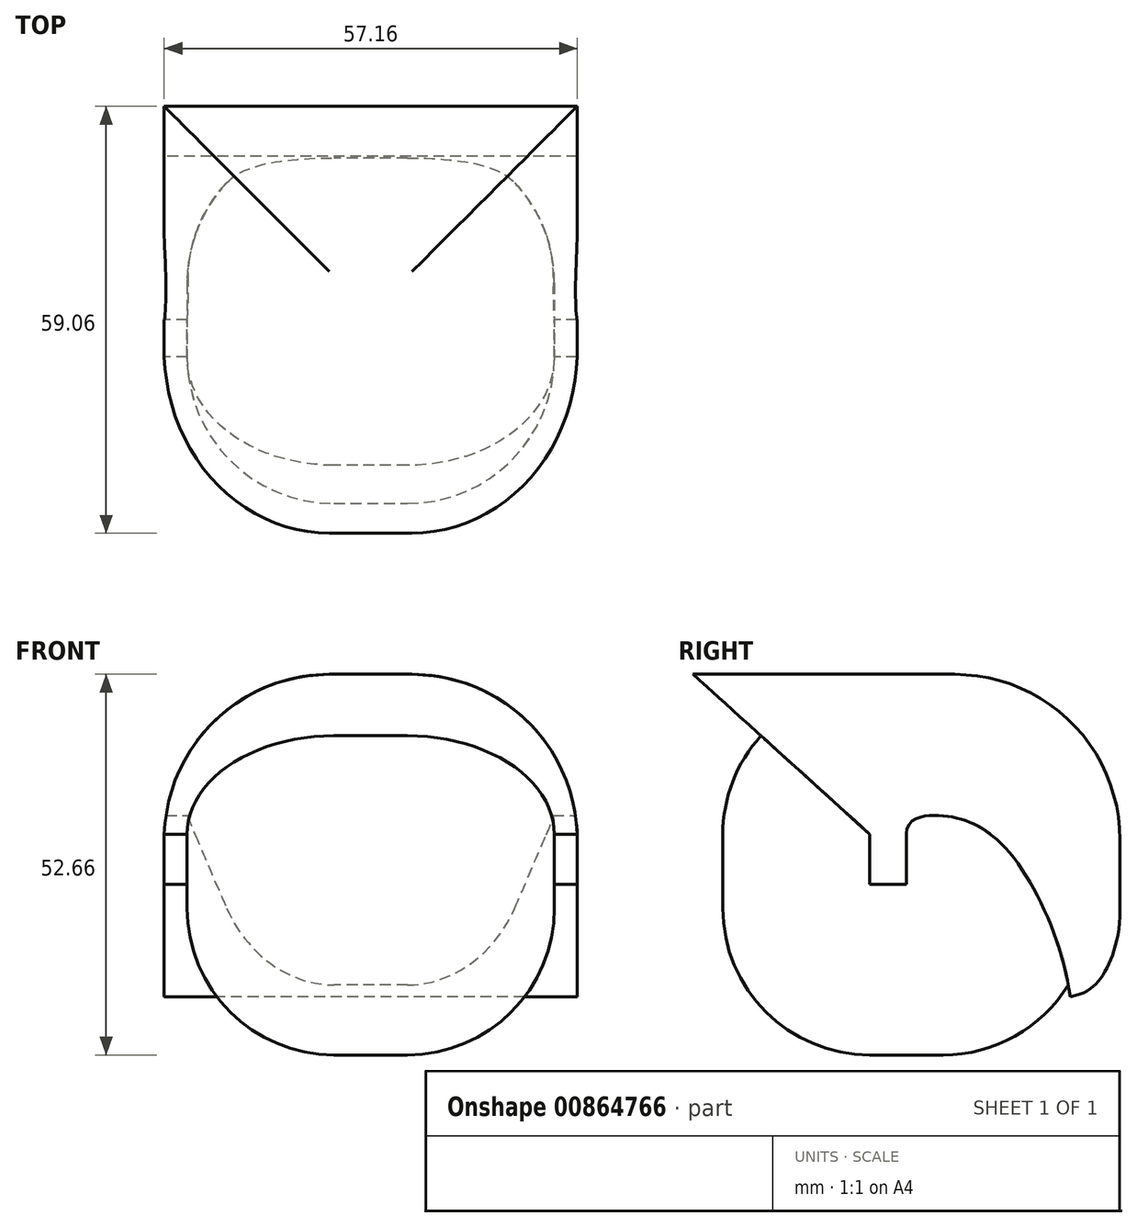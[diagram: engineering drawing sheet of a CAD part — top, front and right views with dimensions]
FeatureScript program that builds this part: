
annotation { "Feature Type Name" : "Feature", "Feature Type Description" : "" }
export const myFeature = defineFeature(function(context is Context, id is Id, definition is map)
    precondition{}
    {
        {
            var Q0;
            Q0=qCreatedBy(makeId("Top.planeOp"),FACE);
            var sketch = newSketch(context, id + "F0", { "sketchPlane" : qUnion([Q0])});
            skLineSegment(sketch, "E0.bottom", {"start": v(-25.4, 25.4) * mm, "end": v(25.4, 25.4) * mm});
            skLineSegment(sketch, "E0.top", {"start": v(-25.4, -25.4) * mm, "end": v(25.4, -25.4) * mm});
            skLineSegment(sketch, "E0.left", {"start": v(-25.4, 25.4) * mm, "end": v(-25.4, -25.4) * mm});
            skLineSegment(sketch, "E0.right", {"start": v(25.4, 25.4) * mm, "end": v(25.4, -25.4) * mm});
            skPoint(sketch, "E0.middle", {"position": v(0, 0) * mm});
            skSolve(sketch);
        }
        {
            var Q0;
            Q0 = qSketchRegion(id + "F0", true);
            extrude(context, id + "F1", {"entities" : qUnion([Q0]), "depth" : 50.8 * mm, "offsetDistance" : 25.4 * mm});
        }
        {
            var Q0;
            Q0=makeQuery(id+"F1.opExtrude","CAP_FACE",FACE,{"disambiguationData":[OSD([sQuery(id+"F0.wireOp",EDGE,"E0.bottom"),sQuery(id+"F0.wireOp",EDGE,"E0.top"),sQuery(id+"F0.wireOp",EDGE,"E0.left"),sQuery(id+"F0.wireOp",EDGE,"E0.right")])],"isStart":false});
            var Q1;
            Q1=makeQuery(id+"F1.opExtrude","SWEPT_FACE",FACE,{"disambiguationData":[OSD([sQuery(id+"F0.wireOp",EDGE,"E0.left")])]});
            var Q2;
            Q2=makeQuery(id+"F1.opExtrude","SWEPT_FACE",FACE,{"disambiguationData":[OSD([sQuery(id+"F0.wireOp",EDGE,"E0.top")])]});
            var Q3;
            Q3=makeQuery(id+"F1.opExtrude","SWEPT_FACE",FACE,{"disambiguationData":[OSD([sQuery(id+"F0.wireOp",EDGE,"E0.right")])]});
            var Q4;
            Q4=makeQuery(id+"F1.opExtrude","CAP_FACE",FACE,{"disambiguationData":[OSD([sQuery(id+"F0.wireOp",EDGE,"E0.bottom"),sQuery(id+"F0.wireOp",EDGE,"E0.top"),sQuery(id+"F0.wireOp",EDGE,"E0.left"),sQuery(id+"F0.wireOp",EDGE,"E0.right")])],"isStart":true});
            var Q5;
            Q5=makeQuery(id+"F1.opExtrude","SWEPT_FACE",FACE,{"disambiguationData":[OSD([sQuery(id+"F0.wireOp",EDGE,"E0.bottom")])]});
            fillet(context, id + "F2", {"entities" : qUnion([Q0, Q1, Q2, Q3, Q4, Q5]), "radius" : 20.32 * mm, "tangentPropagation" : true, "allowEdgeOverflow" : false});
        }
        {
            var Q0;
            Q0=qCreatedBy(makeId("Right.planeOp"),FACE);
            var sketch = newSketch(context, id + "F3", { "sketchPlane" : qUnion([Q0])});
            skLineSegment(sketch, "E1", {"start": v(0, 30.65) * mm, "end": v(0, 23.59) * mm});
            skLineSegment(sketch, "E2", {"start": v(0, 23.59) * mm, "end": v(-5.1, 23.59) * mm});
            skLineSegment(sketch, "E3", {"start": v(-5.1, 23.59) * mm, "end": v(-5.1, 30.55) * mm});
            skFitSpline(sketch, "E4", {"points": [v(0, 30.65) * mm, v(5.8, 33) * mm, v(14.64, 27.5) * mm, v(22.66, 8.04) * mm], "startDerivative": vector(0, 30.14) * mm, "endDerivative": vector(6.46, -47.47) * mm});
            skFitSpline(sketch, "E5", {"points": [v(22.66, 8.04) * mm, v(27.11, 11) * mm, v(29.54, 20.04) * mm], "startDerivative": vector(17.15, 3.72) * mm, "endDerivative": vector(0.03, 21.31) * mm});
            skLineSegment(sketch, "E6", {"start": v(29.54, 20.04) * mm, "end": v(29.54, 52.66) * mm});
            skLineSegment(sketch, "E7", {"start": v(29.54, 52.66) * mm, "end": v(-29.52, 52.66) * mm});
            skLineSegment(sketch, "E8", {"start": v(-5.1, 30.55) * mm, "end": v(-29.52, 52.66) * mm});
            skSolve(sketch);
        }
        {
            var Q0;
            Q0 = qSketchRegion(id + "F3", true);
            extrude(context, id + "F4", {"entities" : qUnion([Q0]), "operationType" : NewBodyOperationType.ADD, "depth" : 28.57 * mm, "offsetDistance" : 25.4 * mm, "hasSecondDirection" : true, "secondDirectionOppositeDirection" : true, "secondDirectionDepth" : 28.57 * mm});
        }
        {
            var Q0;
            Q0=makeQuery(id+"F4.opExtrude","SWEPT_EDGE",EDGE,{"disambiguationData":[OSD([sQuery(id+"F3.wireOp",EDGE,"E6"),sQuery(id+"F3.wireOp",EDGE,"E7")])]});
            var Q1;
            Q1=makeQuery(id+"F4.opExtrude","CAP_EDGE",EDGE,{"disambiguationData":[OSD([sQuery(id+"F3.wireOp",EDGE,"E7")])],"isStart":true});
            var Q2;
            Q2=makeQuery(id+"F4.opExtrude","CAP_EDGE",EDGE,{"disambiguationData":[OSD([sQuery(id+"F3.wireOp",EDGE,"E7")])],"isStart":false});
            fillet(context, id + "F5", {"entities" : qUnion([Q0, Q1, Q2]), "radius" : 22.86 * mm, "tangentPropagation" : true, "allowEdgeOverflow" : false});
        }
    });
